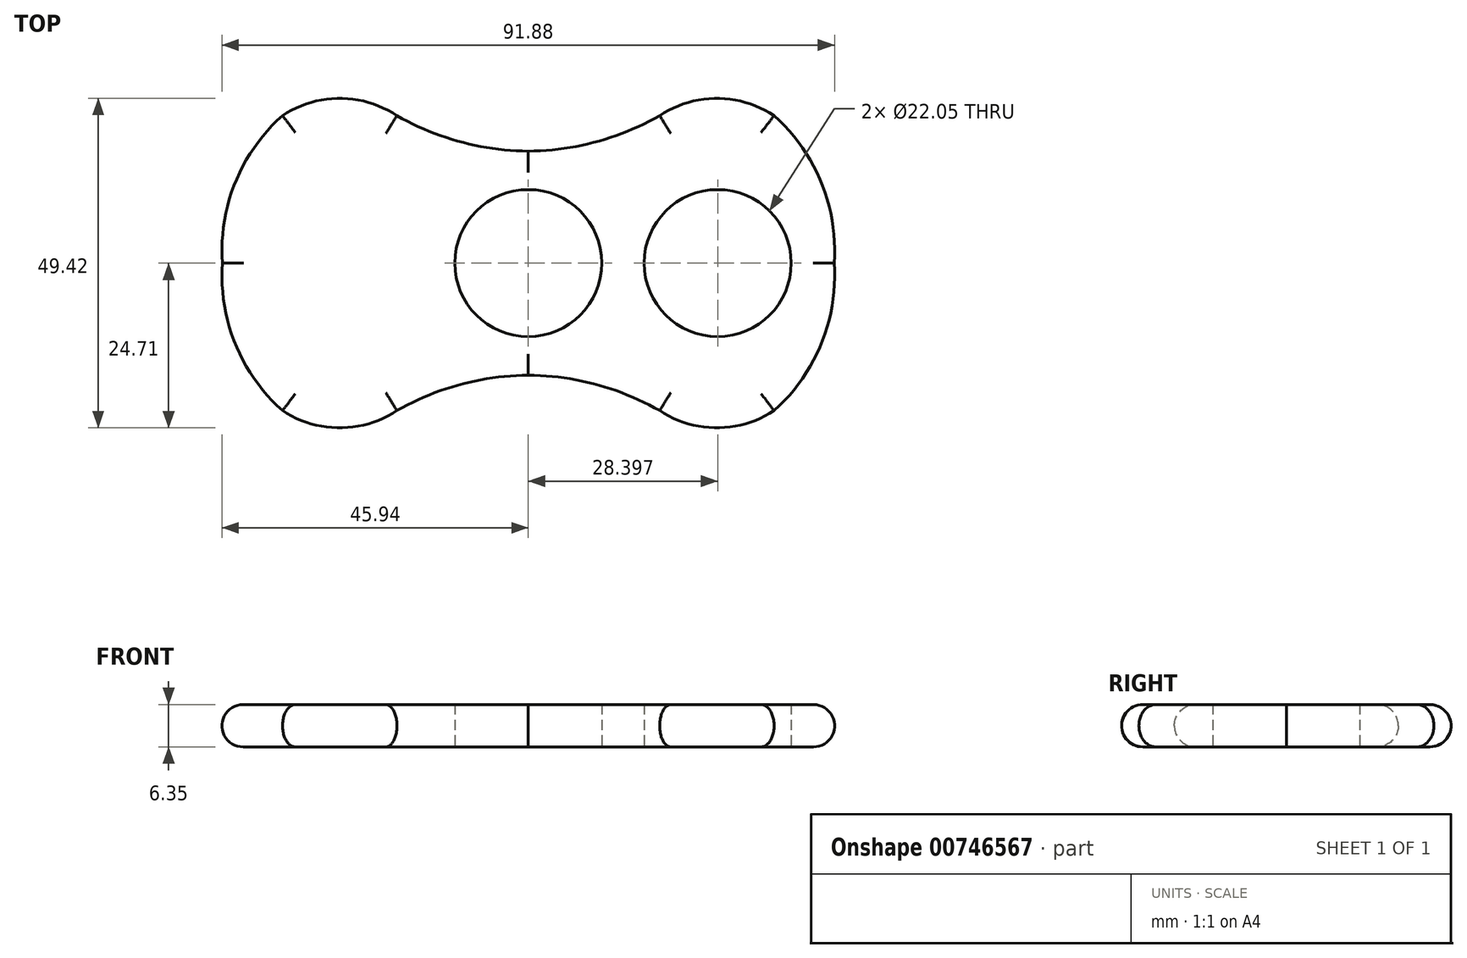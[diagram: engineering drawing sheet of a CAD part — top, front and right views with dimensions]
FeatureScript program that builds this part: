
annotation { "Feature Type Name" : "Feature", "Feature Type Description" : "" }
export const myFeature = defineFeature(function(context is Context, id is Id, definition is map)
    precondition{}
    {
        {
            var Q0;
            Q0=qCreatedBy(makeId("Top.planeOp"),FACE);
            var sketch = newSketch(context, id + "F0", { "sketchPlane" : qUnion([Q0])});
            skCircle(sketch, "E0", {"center": v(0, 0) * mm, "radius": 11.02 * mm});
            skCircle(sketch, "E1", {"center": v(28.4, 0) * mm, "radius": 11.02 * mm});
            skCircle(sketch, "E2.MirrorC", {"center": v(-28.4, 0) * mm, "radius": 11.02 * mm});
            skArc(sketch, "E3", {"start": v(-19.7, 22.12) * mm, "mid": v(-10.19, 18.2) * mm, "end": v(0, 16.8) * mm});
            skArc(sketch, "E4.MirrorCS", {"start": v(19.7, 22.12) * mm, "mid": v(10.19, 18.2) * mm, "end": v(0, 16.8) * mm});
            skArc(sketch, "E5.MirrorCS", {"start": v(19.7, -22.12) * mm, "mid": v(10.19, -18.2) * mm, "end": v(0, -16.8) * mm});
            skArc(sketch, "E6.MirrorCS", {"start": v(-19.7, -22.12) * mm, "mid": v(-10.19, -18.2) * mm, "end": v(0, -16.8) * mm});
            skArc(sketch, "E7", {"start": v(36.86, 22.12) * mm, "mid": v(28.28, 24.7) * mm, "end": v(19.7, 22.12) * mm});
            skArc(sketch, "E8", {"start": v(45.21, -4.36) * mm, "mid": v(44.7, 10.03) * mm, "end": v(36.86, 22.12) * mm});
            skArc(sketch, "E9.MirrorCS", {"start": v(36.86, -22.12) * mm, "mid": v(28.28, -24.7) * mm, "end": v(19.7, -22.12) * mm});
            skArc(sketch, "E10.MirrorCS", {"start": v(45.21, 4.36) * mm, "mid": v(44.7, -10.03) * mm, "end": v(36.86, -22.12) * mm});
            skArc(sketch, "E11.MirrorCS", {"start": v(-36.86, 22.12) * mm, "mid": v(-28.28, 24.7) * mm, "end": v(-19.7, 22.12) * mm});
            skArc(sketch, "E12.MirrorCS", {"start": v(-45.21, -4.36) * mm, "mid": v(-44.7, 10.03) * mm, "end": v(-36.86, 22.12) * mm});
            skArc(sketch, "E13.MirrorCS", {"start": v(-36.86, -22.12) * mm, "mid": v(-28.28, -24.7) * mm, "end": v(-19.7, -22.12) * mm});
            skArc(sketch, "E14.MirrorCS", {"start": v(-45.21, 4.36) * mm, "mid": v(-44.7, -10.03) * mm, "end": v(-36.86, -22.12) * mm});
            skSolve(sketch);
        }
        {
            var Q0;
            Q0=makeQuery(id+"F0.imprint","IMPRINT",FACE,{"disambiguationData":[TD([[makeQuery(id+"F0.imprint","IMPRINT",EDGE,{"derivedFrom":sQuery(id+"F0.wireOp",EDGE,"E3")}),-1.0]])]});
            var Q1;
            Q1=makeQuery(id+"F0.imprint","IMPRINT",FACE,{"disambiguationData":[TD([[makeQuery(id+"F0.imprint","IMPRINT",EDGE,{"derivedFrom":sQuery(id+"F0.wireOp",EDGE,"E5.MirrorCS")}),-1.0]])]});
            var Q2;
            Q2=makeQuery(id+"F0.imprint","IMPRINT",FACE,{"disambiguationData":[TD([[makeQuery(id+"F0.imprint","IMPRINT",EDGE,{"derivedFrom":sQuery(id+"F0.wireOp",EDGE,"E1")}),-1.0]])]});
            var Q3;
            Q3=makeQuery(id+"F0.imprint","IMPRINT",FACE,{"disambiguationData":[TD([[makeQuery(id+"F0.imprint","IMPRINT",EDGE,{"derivedFrom":sQuery(id+"F0.wireOp",EDGE,"E2.MirrorC")}),1.0]])]});
            extrude(context, id + "F1", {"entities" : qUnion([Q0, Q1, Q2, Q3]), "depth" : 6.35 * mm, "offsetDistance" : 25.4 * mm});
        }
        {
            var Q0;
            Q0=makeQuery(id+"F1.opExtrude","CAP_EDGE",EDGE,{"disambiguationData":[OSD([sQuery(id+"F0.wireOp",EDGE,"E4.MirrorCS")])],"isStart":false});
            var Q1;
            Q1=makeQuery(id+"F1.opExtrude","CAP_EDGE",EDGE,{"disambiguationData":[OSD([sQuery(id+"F0.wireOp",EDGE,"E7")])],"isStart":false});
            var Q2;
            Q2=makeQuery(id+"F1.opExtrude","CAP_EDGE",EDGE,{"disambiguationData":[OSD([sQuery(id+"F0.wireOp",EDGE,"E8")])],"isStart":false});
            var Q3;
            Q3=makeQuery(id+"F1.opExtrude","CAP_EDGE",EDGE,{"disambiguationData":[OSD([sQuery(id+"F0.wireOp",EDGE,"E10.MirrorCS")])],"isStart":false});
            var Q4;
            Q4=makeQuery(id+"F1.opExtrude","CAP_EDGE",EDGE,{"disambiguationData":[OSD([sQuery(id+"F0.wireOp",EDGE,"E9.MirrorCS")])],"isStart":false});
            var Q5;
            Q5=makeQuery(id+"F1.opExtrude","CAP_EDGE",EDGE,{"disambiguationData":[OSD([sQuery(id+"F0.wireOp",EDGE,"E5.MirrorCS")])],"isStart":false});
            var Q6;
            Q6=makeQuery(id+"F1.opExtrude","CAP_EDGE",EDGE,{"disambiguationData":[OSD([sQuery(id+"F0.wireOp",EDGE,"E6.MirrorCS")])],"isStart":false});
            var Q7;
            Q7=makeQuery(id+"F1.opExtrude","CAP_EDGE",EDGE,{"disambiguationData":[OSD([sQuery(id+"F0.wireOp",EDGE,"E13.MirrorCS")])],"isStart":false});
            var Q8;
            Q8=makeQuery(id+"F1.opExtrude","CAP_EDGE",EDGE,{"disambiguationData":[OSD([sQuery(id+"F0.wireOp",EDGE,"E14.MirrorCS")])],"isStart":false});
            var Q9;
            Q9=makeQuery(id+"F1.opExtrude","CAP_EDGE",EDGE,{"disambiguationData":[OSD([sQuery(id+"F0.wireOp",EDGE,"E12.MirrorCS")])],"isStart":false});
            var Q10;
            Q10=makeQuery(id+"F1.opExtrude","CAP_EDGE",EDGE,{"disambiguationData":[OSD([sQuery(id+"F0.wireOp",EDGE,"E11.MirrorCS")])],"isStart":false});
            var Q11;
            Q11=makeQuery(id+"F1.opExtrude","CAP_EDGE",EDGE,{"disambiguationData":[OSD([sQuery(id+"F0.wireOp",EDGE,"E3")])],"isStart":true});
            fillet(context, id + "F2", {"entities" : qUnion([Q0, Q1, Q2, Q3, Q4, Q5, Q6, Q7, Q8, Q9, Q10, Q11]), "radius" : 3.17 * mm, "tangentPropagation" : true, "allowEdgeOverflow" : false});
        }
        {
            var Q0;
            Q0=makeQuery(id+"F1.opExtrude","CAP_EDGE",EDGE,{"disambiguationData":[OSD([sQuery(id+"F0.wireOp",EDGE,"E5.MirrorCS")])],"isStart":true});
            var Q1;
            Q1=makeQuery(id+"F1.opExtrude","CAP_EDGE",EDGE,{"disambiguationData":[OSD([sQuery(id+"F0.wireOp",EDGE,"E9.MirrorCS")])],"isStart":true});
            var Q2;
            Q2=makeQuery(id+"F1.opExtrude","CAP_EDGE",EDGE,{"disambiguationData":[OSD([sQuery(id+"F0.wireOp",EDGE,"E10.MirrorCS")])],"isStart":true});
            var Q3;
            Q3=makeQuery(id+"F1.opExtrude","CAP_EDGE",EDGE,{"disambiguationData":[OSD([sQuery(id+"F0.wireOp",EDGE,"E8")])],"isStart":true});
            var Q4;
            Q4=makeQuery(id+"F1.opExtrude","CAP_EDGE",EDGE,{"disambiguationData":[OSD([sQuery(id+"F0.wireOp",EDGE,"E7")])],"isStart":true});
            var Q5;
            Q5=makeQuery(id+"F1.opExtrude","CAP_EDGE",EDGE,{"disambiguationData":[OSD([sQuery(id+"F0.wireOp",EDGE,"E4.MirrorCS")])],"isStart":true});
            var Q6;
            Q6=makeQuery(id+"F1.opExtrude","CAP_EDGE",EDGE,{"disambiguationData":[OSD([sQuery(id+"F0.wireOp",EDGE,"E3")])],"isStart":true});
            var Q7;
            Q7=makeQuery(id+"F1.opExtrude","CAP_EDGE",EDGE,{"disambiguationData":[OSD([sQuery(id+"F0.wireOp",EDGE,"E11.MirrorCS")])],"isStart":true});
            var Q8;
            Q8=makeQuery(id+"F1.opExtrude","CAP_EDGE",EDGE,{"disambiguationData":[OSD([sQuery(id+"F0.wireOp",EDGE,"E12.MirrorCS")])],"isStart":true});
            var Q9;
            Q9=makeQuery(id+"F1.opExtrude","CAP_EDGE",EDGE,{"disambiguationData":[OSD([sQuery(id+"F0.wireOp",EDGE,"E14.MirrorCS")])],"isStart":true});
            var Q10;
            Q10=makeQuery(id+"F1.opExtrude","CAP_EDGE",EDGE,{"disambiguationData":[OSD([sQuery(id+"F0.wireOp",EDGE,"E13.MirrorCS")])],"isStart":true});
            var Q11;
            Q11=makeQuery(id+"F1.opExtrude","CAP_EDGE",EDGE,{"disambiguationData":[OSD([sQuery(id+"F0.wireOp",EDGE,"E6.MirrorCS")])],"isStart":true});
            fillet(context, id + "F3", {"entities" : qUnion([Q0, Q1, Q2, Q3, Q4, Q5, Q6, Q7, Q8, Q9, Q10, Q11]), "radius" : 3.17 * mm, "tangentPropagation" : true, "allowEdgeOverflow" : false});
        }
    });
